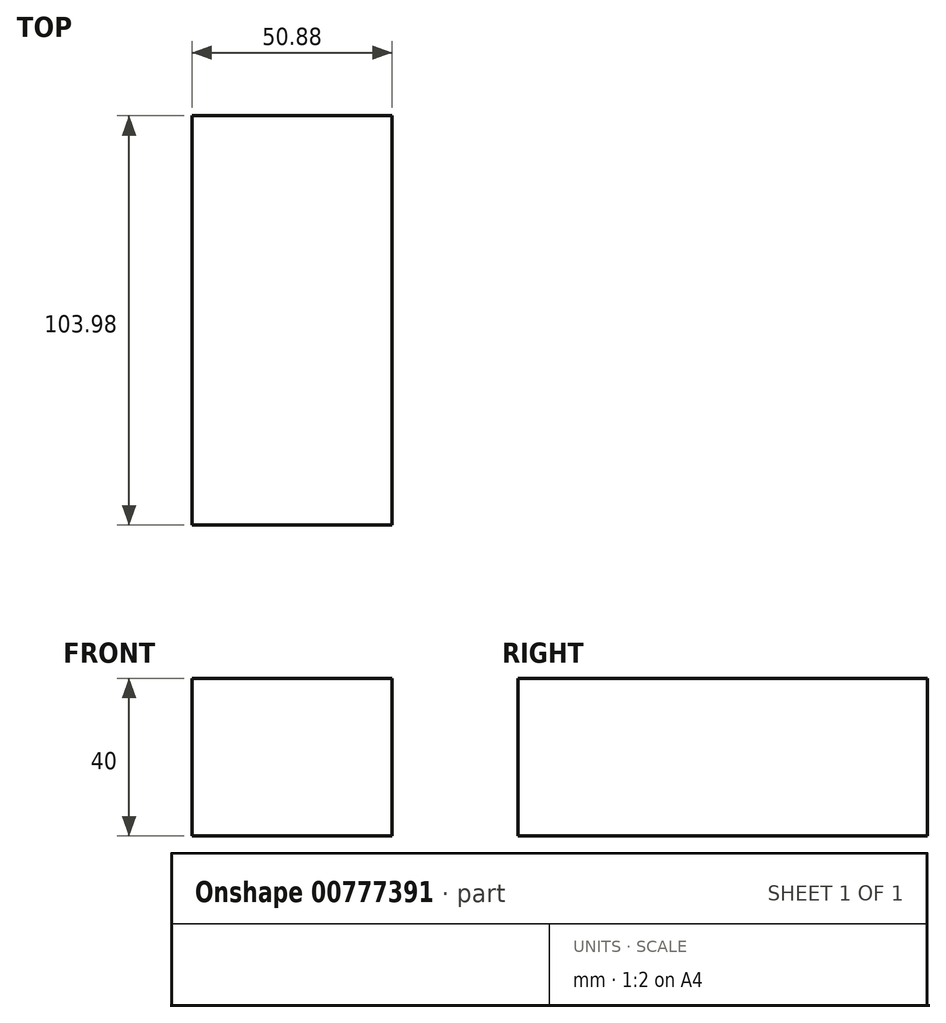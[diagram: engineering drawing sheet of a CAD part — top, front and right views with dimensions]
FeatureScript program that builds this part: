
annotation { "Feature Type Name" : "Feature", "Feature Type Description" : "" }
export const myFeature = defineFeature(function(context is Context, id is Id, definition is map)
    precondition{}
    {
        {
            var Q0;
            Q0=qCreatedBy(makeId("Top.planeOp"),FACE);
            var sketch = newSketch(context, id + "F0", { "sketchPlane" : qUnion([Q0])});
            skLineSegment(sketch, "E0.bottom", {"start": v(-65.1, 58.5) * mm, "end": v(36.67, 58.5) * mm});
            skLineSegment(sketch, "E0.top", {"start": v(-65.1, -45.48) * mm, "end": v(36.67, -45.48) * mm});
            skLineSegment(sketch, "E0.left", {"start": v(-65.1, 58.5) * mm, "end": v(-65.1, -45.48) * mm});
            skLineSegment(sketch, "E0.right", {"start": v(36.67, 58.5) * mm, "end": v(36.67, -45.48) * mm});
            skLineSegment(sketch, "E1.bottom", {"start": v(-14.21, 58.5) * mm, "end": v(-65.1, 58.5) * mm});
            skLineSegment(sketch, "E1.top", {"start": v(-14.21, -45.48) * mm, "end": v(-65.1, -45.48) * mm});
            skLineSegment(sketch, "E1.left", {"start": v(-14.21, 58.5) * mm, "end": v(-14.21, -45.48) * mm});
            skSolve(sketch);
        }
        {
            var Q0;
            {var subQ2=sQuery(id+"F0.wireOp",EDGE,"E0.left");Q0=makeQuery(id+"F0.imprint","IMPRINT",FACE,{"disambiguationData":[TD([[makeQuery(id+"F0.imprint","IMPRINT",EDGE,{"derivedFrom":subQ2}),1.0]])]});}
            extrude(context, id + "F1", {"entities" : qUnion([Q0]), "depth" : 40 * mm, "offsetDistance" : 25.4 * mm});
        }
    });
